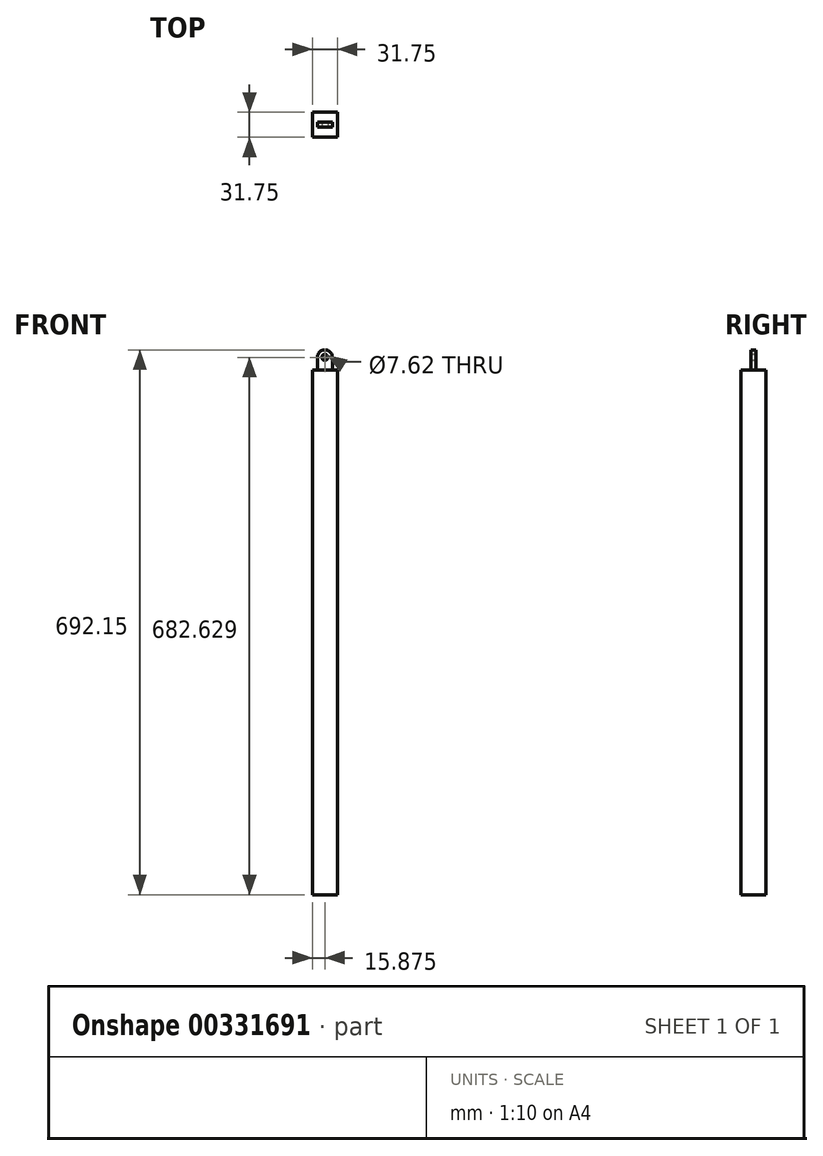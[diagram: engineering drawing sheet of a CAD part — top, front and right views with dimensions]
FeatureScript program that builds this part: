
annotation { "Feature Type Name" : "Feature", "Feature Type Description" : "" }
export const myFeature = defineFeature(function(context is Context, id is Id, definition is map)
    precondition{}
    {
        {
            var Q0;
            Q0=qCreatedBy(makeId("Front.planeOp"),FACE);
            var sketch = newSketch(context, id + "F0", { "sketchPlane" : qUnion([Q0])});
            skLineSegment(sketch, "E0.bottom", {"start": v(-31.75, 460.96) * mm, "end": v(0, 460.96) * mm});
            skLineSegment(sketch, "E0.top", {"start": v(-31.75, -205.79) * mm, "end": v(0, -205.79) * mm});
            skLineSegment(sketch, "E0.left", {"start": v(-31.75, 460.96) * mm, "end": v(-31.75, -205.79) * mm});
            skLineSegment(sketch, "E0.right", {"start": v(0, 460.96) * mm, "end": v(0, -205.79) * mm});
            skSolve(sketch);
        }
        {
            var Q0;
            Q0=makeQuery(id+"F0.imprint","IMPRINT",FACE,{"disambiguationData":[TD([[makeQuery(id+"F0.imprint","IMPRINT",EDGE,{"derivedFrom":sQuery(id+"F0.wireOp",EDGE,"E0.bottom")}),-1.0]])]});
            extrude(context, id + "F1", {"entities" : qUnion([Q0]), "oppositeDirection" : true, "depth" : 31.75 * mm});
        }
        {
            var Q0;
            Q0=makeQuery(id+"F1.opExtrude","SWEPT_FACE",FACE,{"disambiguationData":[OSD([sQuery(id+"F0.wireOp",EDGE,"E0.bottom")])]});
            var sketch = newSketch(context, id + "F2", { "sketchPlane" : qUnion([Q0])});
            skLineSegment(sketch, "E1.bottom", {"start": v(-25.4, 19.05) * mm, "end": v(-6.35, 19.05) * mm});
            skLineSegment(sketch, "E1.top", {"start": v(-25.4, 12.7) * mm, "end": v(-6.35, 12.7) * mm});
            skLineSegment(sketch, "E1.left", {"start": v(-25.4, 19.05) * mm, "end": v(-25.4, 12.7) * mm});
            skLineSegment(sketch, "E1.right", {"start": v(-6.35, 19.05) * mm, "end": v(-6.35, 12.7) * mm});
            skSolve(sketch);
        }
        {
            var Q0;
            Q0=makeQuery(id+"F2.imprint","IMPRINT",FACE,{"disambiguationData":[TD([[makeQuery(id+"F2.imprint","IMPRINT",EDGE,{"derivedFrom":sQuery(id+"F2.wireOp",EDGE,"E1.bottom")}),-1.0]])]});
            extrude(context, id + "F3", {"entities" : qUnion([Q0]), "operationType" : NewBodyOperationType.ADD, "depth" : 25.4 * mm});
        }
        {
            var Q0;
            Q0=makeQuery(id+"F3.opExtrude","CAP_EDGE",EDGE,{"disambiguationData":[OSD([sQuery(id+"F2.wireOp",EDGE,"E1.right")])],"isStart":false});
            var Q1;
            Q1=makeQuery(id+"F3.opExtrude","CAP_EDGE",EDGE,{"disambiguationData":[OSD([sQuery(id+"F2.wireOp",EDGE,"E1.left")])],"isStart":false});
            fillet(context, id + "F4", {"entities" : qUnion([Q0, Q1]), "radius" : 9.52 * mm, "tangentPropagation" : true, "allowEdgeOverflow" : false});
        }
        {
            var Q0;
            Q0=makeQuery(id+"F3.opExtrude","SWEPT_FACE",FACE,{"disambiguationData":[OSD([sQuery(id+"F2.wireOp",EDGE,"E1.top")])]});
            var sketch = newSketch(context, id + "F5", { "sketchPlane" : qUnion([Q0])});
            skCircle(sketch, "E2", {"center": v(-15.88, 476.84) * mm, "radius": 3.81 * mm});
            skSolve(sketch);
        }
        {
            var Q0;
            Q0=qSketchRegion(id+"F5",true);
            extrude(context, id + "F6", {"entities" : qUnion([Q0]), "operationType" : NewBodyOperationType.REMOVE, "oppositeDirection" : true, "depth" : 6.35 * mm});
        }
    });
